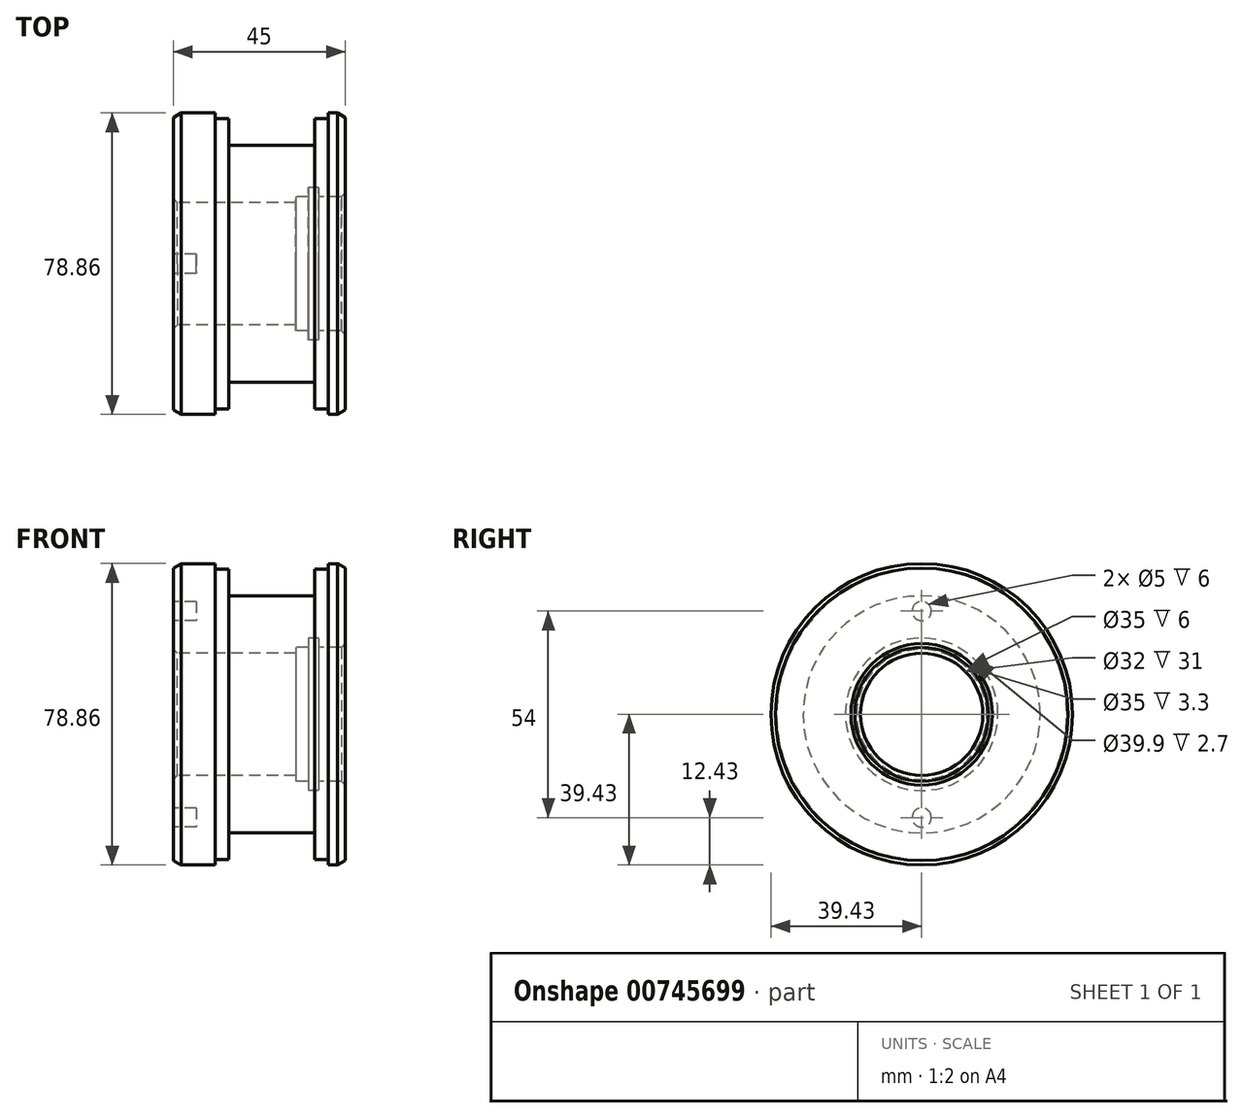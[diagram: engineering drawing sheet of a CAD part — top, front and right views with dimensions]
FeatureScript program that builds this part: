
annotation { "Feature Type Name" : "Feature", "Feature Type Description" : "" }
export const myFeature = defineFeature(function(context is Context, id is Id, definition is map)
    precondition{}
    {
        {
            var Q0;
            Q0=qCreatedBy(makeId("Front.planeOp"),FACE);
            var sketch = newSketch(context, id + "F0", { "sketchPlane" : qUnion([Q0])});
            skLineSegment(sketch, "E0", {"start": v(-265.54, 0) * mm, "end": v(321.9, 0) * mm, "construction": true});
            skLineSegment(sketch, "E1", {"start": v(-141.26, 17.5) * mm, "end": v(-141.26, 39.42) * mm});
            skLineSegment(sketch, "E2", {"start": v(-141.26, 39.42) * mm, "end": v(-145.66, 39.42) * mm});
            skLineSegment(sketch, "E3", {"start": v(-145.66, 39.42) * mm, "end": v(-145.66, 38) * mm});
            skLineSegment(sketch, "E4", {"start": v(-145.66, 38) * mm, "end": v(-149.26, 38) * mm});
            skLineSegment(sketch, "E5", {"start": v(-149.26, 38) * mm, "end": v(-149.26, 31) * mm});
            skLineSegment(sketch, "E6", {"start": v(-149.26, 31) * mm, "end": v(-171.76, 31) * mm});
            skLineSegment(sketch, "E7", {"start": v(-171.76, 31) * mm, "end": v(-171.76, 38) * mm});
            skLineSegment(sketch, "E8", {"start": v(-171.76, 38) * mm, "end": v(-175.36, 38) * mm});
            skLineSegment(sketch, "E9", {"start": v(-175.36, 38) * mm, "end": v(-175.36, 39.42) * mm});
            skLineSegment(sketch, "E10", {"start": v(-175.36, 39.42) * mm, "end": v(-186.26, 39.42) * mm});
            skLineSegment(sketch, "E11", {"start": v(-186.26, 39.42) * mm, "end": v(-186.26, 16) * mm});
            skLineSegment(sketch, "E12", {"start": v(-141.26, 17.5) * mm, "end": v(-148.26, 17.5) * mm});
            skLineSegment(sketch, "E13", {"start": v(-154.26, 16) * mm, "end": v(-186.26, 16) * mm});
            skLineSegment(sketch, "E14", {"start": v(-154.26, 17.5) * mm, "end": v(-154.26, 16) * mm});
            skPoint(sketch, "E15.orphan", {"position": v(-186.26, 0) * mm});
            skLineSegment(sketch, "E16", {"start": v(-150.96, 19.95) * mm, "end": v(-148.26, 19.95) * mm});
            skLineSegment(sketch, "E17", {"start": v(-148.26, 19.95) * mm, "end": v(-148.26, 17.5) * mm});
            skLineSegment(sketch, "E18", {"start": v(-150.96, 19.95) * mm, "end": v(-150.96, 17.5) * mm});
            skLineSegment(sketch, "E19.trimOffspring", {"start": v(-150.96, 17.5) * mm, "end": v(-154.26, 17.5) * mm});
            skSolve(sketch);
        }
        {
            var Q0;
            Q0=makeQuery(id+"F0.imprint","IMPRINT",FACE,{"disambiguationData":[TD([[makeQuery(id+"F0.imprint","IMPRINT",EDGE,{"derivedFrom":sQuery(id+"F0.wireOp",EDGE,"E1")}),1.0]])]});
            var Q1;
            Q1=sQuery(id+"F0.wireOp",EDGE,"E0");
            revolve(context, id + "F1", {"surfaceOperationType" : NewSurfaceOperationType.NEW, "entities" : qUnion([Q0]), "axis" : qUnion([Q1]), "revolveType" : RevolveType.FULL});
        }
        {
            var Q0;
            Q0=makeQuery(id+"F1.opRevolve","SWEPT_EDGE",EDGE,{"disambiguationData":[OSD([sQuery(id+"F0.wireOp",EDGE,"E10"),sQuery(id+"F0.wireOp",EDGE,"E11")])]});
            chamfer(context, id + "F2", {"entities" : qUnion([Q0]), "chamferType" : ChamferType.OFFSET_ANGLE, "width" : 2 * mm, "oppositeDirection" : true, "angle" : 30 * degree, "tangentPropagation" : true});
        }
        {
            var Q0;
            Q0=makeQuery(id+"F1.opRevolve","SWEPT_FACE",FACE,{"disambiguationData":[OSD([sQuery(id+"F0.wireOp",EDGE,"E11")])]});
            var sketch = newSketch(context, id + "F3", { "sketchPlane" : qUnion([Q0])});
            skCircle(sketch, "E20", {"center": v(0, 27) * mm, "radius": 2.5 * mm});
            skCircle(sketch, "E21", {"center": v(0, -27) * mm, "radius": 2.5 * mm});
            skCircle(sketch, "E22", {"center": v(0, 0) * mm, "radius": 27 * mm, "construction": true});
            skSolve(sketch);
        }
        {
            var Q0;
            Q0=makeQuery(id+"F3.imprint","IMPRINT",FACE,{"disambiguationData":[TD([[makeQuery(id+"F3.imprint","IMPRINT",EDGE,{"derivedFrom":sQuery(id+"F3.wireOp",EDGE,"E20")}),1.0]])]});
            var Q1;
            Q1=makeQuery(id+"F3.imprint","IMPRINT",FACE,{"disambiguationData":[TD([[makeQuery(id+"F3.imprint","IMPRINT",EDGE,{"derivedFrom":sQuery(id+"F3.wireOp",EDGE,"E21")}),1.0]])]});
            extrude(context, id + "F4", {"entities" : qUnion([Q0, Q1]), "operationType" : NewBodyOperationType.REMOVE, "oppositeDirection" : true, "depth" : 6 * mm, "offsetDistance" : 25 * mm});
        }
        {
            var Q0;
            Q0=makeQuery(id+"F1.opRevolve","SWEPT_EDGE",EDGE,{"disambiguationData":[OSD([sQuery(id+"F0.wireOp",EDGE,"E1"),sQuery(id+"F0.wireOp",EDGE,"E2")])]});
            chamfer(context, id + "F5", {"entities" : qUnion([Q0]), "chamferType" : ChamferType.OFFSET_ANGLE, "width" : 2 * mm, "oppositeDirection" : false, "angle" : 30 * degree, "tangentPropagation" : true});
        }
        {
            var Q0;
            Q0=makeQuery(id+"F1.opRevolve","SWEPT_EDGE",EDGE,{"disambiguationData":[OSD([sQuery(id+"F0.wireOp",EDGE,"E11"),sQuery(id+"F0.wireOp",EDGE,"E13")])]});
            var Q1;
            Q1=makeQuery(id+"F1.opRevolve","SWEPT_EDGE",EDGE,{"disambiguationData":[OSD([sQuery(id+"F0.wireOp",EDGE,"E1"),sQuery(id+"F0.wireOp",EDGE,"E12")])]});
            chamfer(context, id + "F6", {"entities" : qUnion([Q0, Q1]), "width" : 1 * mm, "tangentPropagation" : true});
        }
    });
